# Revit family: Fireplace-Chimney-Assy_Basic
name_source: partatom
category: Mechanical Equipment
units: mm (PartAtom-declared; Revit-internal decimal feet)

## family parameters
Always vertical = Yes
Classification Number = 23.70.70.21.14
Cut with Voids When Loaded = No
Maintain Annotation Orientation = No
Part Type = Normal
Room Calculation Point = No
Round Connector Dimension = Use Diameter
Shared = No
Work Plane-Based = No

## types (1)
- Fireplace-Chimney-Assy_Basic
    Assembly Code = D3020
    Chimney Cap Height = 0' - 4"
    Chimney Cap Material = Concrete - Cast-in-Place Concrete
    Chimney Height_TO Cap = 20' - 0"
    Chimney Structure Material = Masonry - Concrete Masonry Units
    Construction Details = http://www.arcat.com
    Default Elevation = 0' - 0"
    Description = Masonry Chimney and Fireplace Assembly
    Expected Lifespan (Years) = 75
    Finished Face Material = Masonry - Brick
    Firebox Width = 3' - 0"
    Flue Extension = 0' - 6"
    Flue Length = 20' - 6"
    FlueRad = 0' - 8"
    Green Building - LEED = http://www.arcat.com
    Keynote = 04500
    Maintenance Schedule (Months) = 0
    Manufacturer = Generic
    Manufacturer Fax = (203) 939-2444
    Manufacturer Website = http://www.arcat.com
    Model = Generic
    Outer Wall Thickness = 0' - 4"
    Outside Wall to Flue CL = 2' - 0"
    Product Data = http://www.arcat.com
    Product Properties = http://www.arcat.com
    Specification = http://www.arcat.com
    TO Smoke Chamber = 4' - 4"
    URL = http://www.arcat.com
    Warranty Duration (Years) = 0

## geometry (parser evidence)
native form markers: Sweep x11
no freeform markers — native parametric forms only
